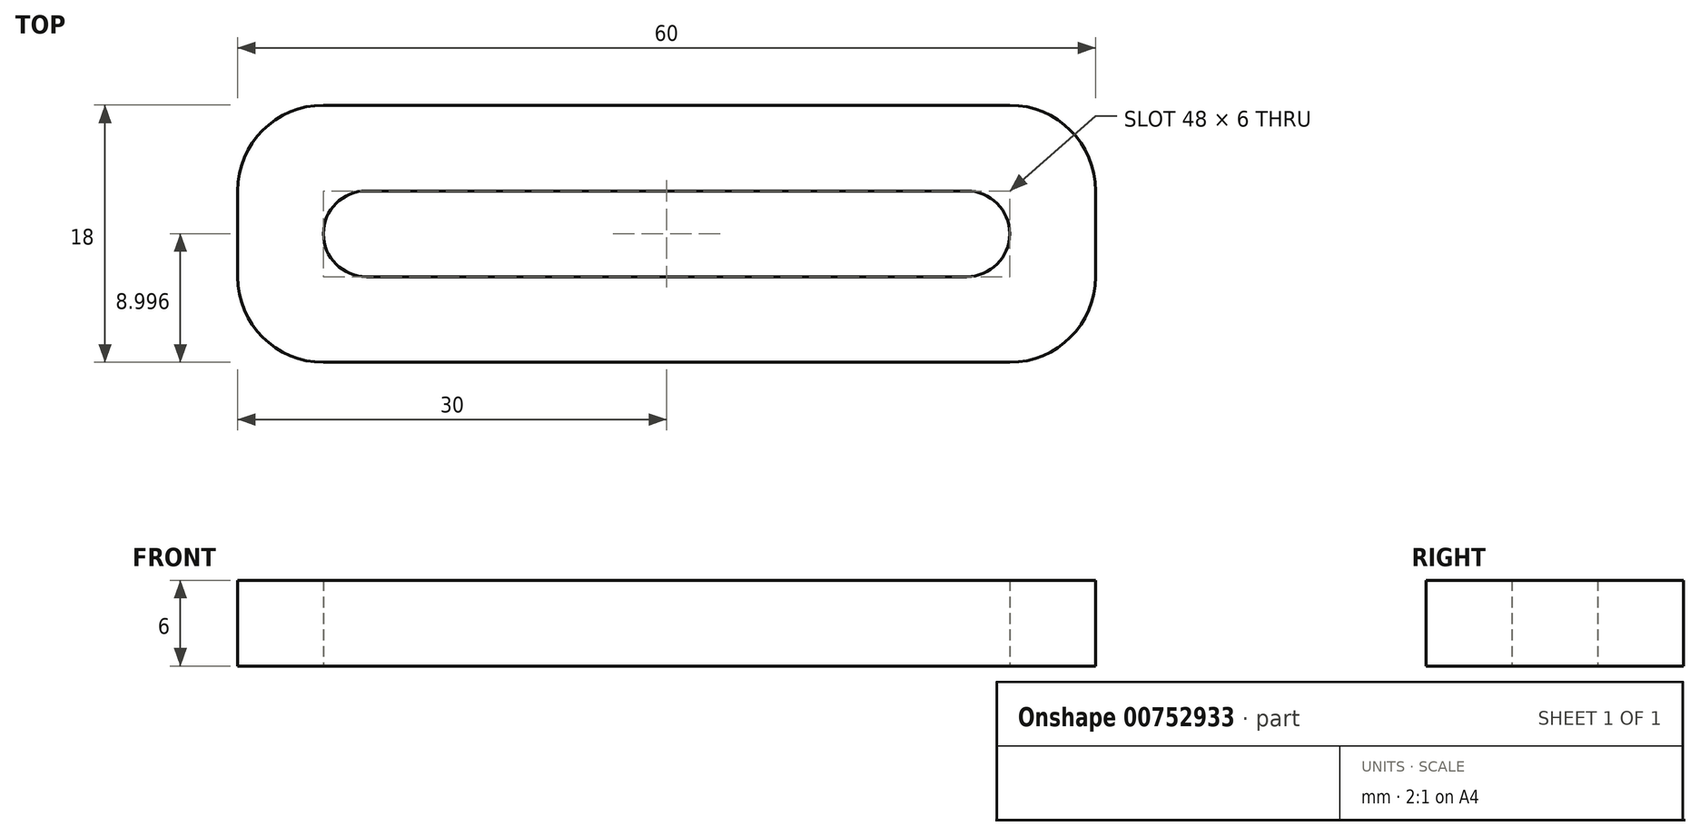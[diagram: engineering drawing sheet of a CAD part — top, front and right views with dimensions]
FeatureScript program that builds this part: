
annotation { "Feature Type Name" : "Feature", "Feature Type Description" : "" }
export const myFeature = defineFeature(function(context is Context, id is Id, definition is map)
    precondition{}
    {
        {
            var Q0;
            Q0=qCreatedBy(makeId("Top.planeOp"),FACE);
            var sketch = newSketch(context, id + "F0", { "sketchPlane" : qUnion([Q0])});
            skLineSegment(sketch, "E0.bottom", {"start": v(-33.54, 7.79) * mm, "end": v(14.46, 7.79) * mm});
            skLineSegment(sketch, "E0.top", {"start": v(-33.54, 25.79) * mm, "end": v(14.46, 25.79) * mm});
            skLineSegment(sketch, "E0.left", {"start": v(-39.54, 13.79) * mm, "end": v(-39.54, 19.79) * mm});
            skLineSegment(sketch, "E0.right", {"start": v(20.46, 13.79) * mm, "end": v(20.46, 19.79) * mm});
            skLineSegment(sketch, "E1", {"start": v(-39.54, 16.79) * mm, "end": v(-30.54, 16.79) * mm, "construction": true});
            skLineSegment(sketch, "E2", {"start": v(-30.54, 16.79) * mm, "end": v(11.46, 16.79) * mm, "construction": true});
            skLineSegment(sketch, "E3", {"start": v(11.46, 16.79) * mm, "end": v(20.46, 16.79) * mm, "construction": true});
            skArc(sketch, "E4.0.startCap", {"start": v(-30.54, 13.79) * mm, "mid": v(-33.54, 16.79) * mm, "end": v(-30.54, 19.79) * mm});
            skArc(sketch, "E4.0.endCap", {"start": v(11.46, 19.79) * mm, "mid": v(14.46, 16.79) * mm, "end": v(11.46, 13.79) * mm});
            skLineSegment(sketch, "E4.0.left", {"start": v(-30.54, 19.79) * mm, "end": v(11.46, 19.79) * mm});
            skLineSegment(sketch, "E4.0.right", {"start": v(-30.54, 13.79) * mm, "end": v(11.46, 13.79) * mm});
            skPoint(sketch, "E5.visualSharp", {"position": v(-39.54, 25.79) * mm});
            skArc(sketch, "E5.filletArc", {"start": v(-33.54, 25.79) * mm, "mid": v(-37.78, 24.03) * mm, "end": v(-39.54, 19.79) * mm});
            skPoint(sketch, "E6.visualSharp", {"position": v(-39.54, 7.79) * mm});
            skArc(sketch, "E6.filletArc", {"start": v(-39.54, 13.79) * mm, "mid": v(-37.78, 9.54) * mm, "end": v(-33.54, 7.79) * mm});
            skPoint(sketch, "E7.visualSharp", {"position": v(20.46, 7.79) * mm});
            skArc(sketch, "E7.filletArc", {"start": v(14.46, 7.79) * mm, "mid": v(18.7, 9.54) * mm, "end": v(20.46, 13.79) * mm});
            skPoint(sketch, "E8.visualSharp", {"position": v(20.46, 25.79) * mm});
            skArc(sketch, "E8.filletArc", {"start": v(20.46, 19.79) * mm, "mid": v(18.7, 24.03) * mm, "end": v(14.46, 25.79) * mm});
            skSolve(sketch);
        }
        {
            var Q0;
            Q0=makeQuery(id+"F0.imprint","IMPRINT",FACE,{"disambiguationData":[TD([[makeQuery(id+"F0.imprint","IMPRINT",EDGE,{"derivedFrom":sQuery(id+"F0.wireOp",EDGE,"E0.bottom")}),1.0]])]});
            extrude(context, id + "F1", {"entities" : qUnion([Q0]), "depth" : 6 * mm, "offsetDistance" : 25 * mm});
        }
    });
